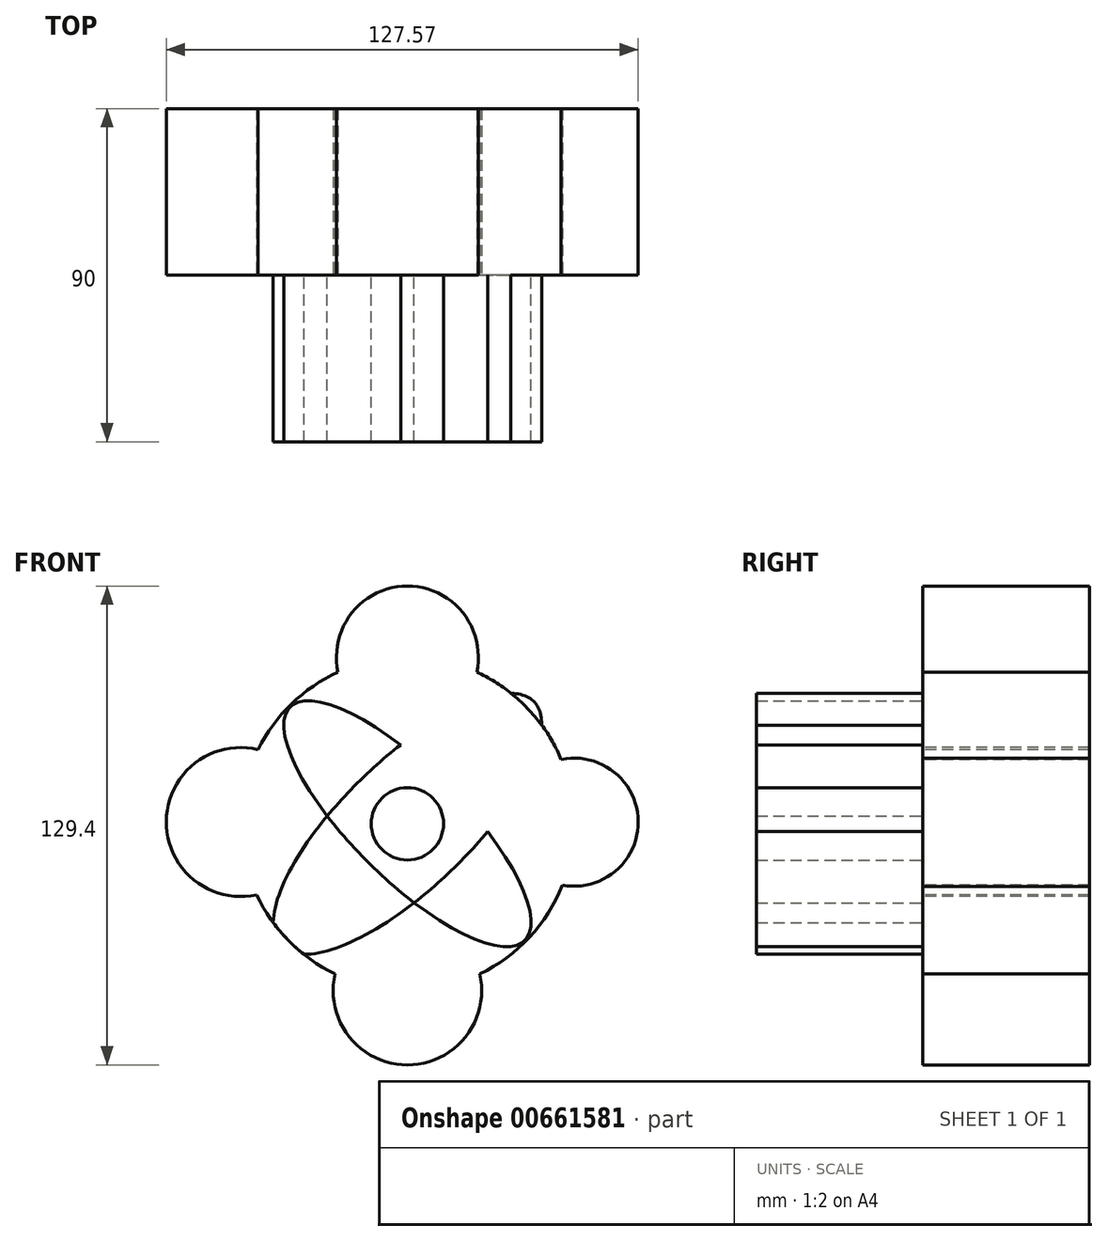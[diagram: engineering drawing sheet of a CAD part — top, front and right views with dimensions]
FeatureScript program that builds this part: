
annotation { "Feature Type Name" : "Feature", "Feature Type Description" : "" }
export const myFeature = defineFeature(function(context is Context, id is Id, definition is map)
    precondition{}
    {
        {
            var Q0;
            Q0=qCreatedBy(makeId("Front.planeOp"),FACE);
            var sketch = newSketch(context, id + "F0", { "sketchPlane" : qUnion([Q0])});
            skCircle(sketch, "E0", {"center": v(0, 0) * mm, "radius": 9.77 * mm});
            skPoint(sketch, "E1", {"position": v(0, 45) * mm});
            skPoint(sketch, "E2", {"position": v(45, 0) * mm});
            skPoint(sketch, "E3", {"position": v(0, -45) * mm});
            skPoint(sketch, "E4", {"position": v(-45, 0) * mm});
            skLineSegment(sketch, "E5", {"start": v(0, 0) * mm, "end": v(0, 45) * mm});
            skLineSegment(sketch, "E6", {"start": v(0, 0) * mm, "end": v(0, -45) * mm});
            skLineSegment(sketch, "E7", {"start": v(0, 0) * mm, "end": v(45, 0) * mm});
            skLineSegment(sketch, "E8", {"start": v(0, 0) * mm, "end": v(-45, 0) * mm});
            skSolve(sketch);
        }
        {
            var Q0;
            Q0=qCreatedBy(makeId("Front.planeOp"),FACE);
            var sketch = newSketch(context, id + "F1", { "sketchPlane" : qUnion([Q0])});
            skArc(sketch, "E9", {"start": v(0, 45.02) * mm, "mid": v(31.83, 31.83) * mm, "end": v(45.02, 0) * mm});
            skArc(sketch, "E10", {"start": v(0, 45.02) * mm, "mid": v(-31.83, 31.83) * mm, "end": v(-45.02, 0) * mm});
            skArc(sketch, "E11", {"start": v(-45.02, 0) * mm, "mid": v(-31.83, -31.83) * mm, "end": v(0, -45.02) * mm});
            skArc(sketch, "E12", {"start": v(0, -45.02) * mm, "mid": v(31.83, -31.83) * mm, "end": v(45.02, 0) * mm});
            skEllipse(sketch, "E13", {"center": v(0, 0) * mm, "majorRadius": 44.74 * mm, "minorRadius": 14.86 * mm, "majorAxis": v(-0.7, 0.7)});
            skEllipse(sketch, "E14", {"center": v(0, 0) * mm, "majorRadius": 47.54 * mm, "minorRadius": 17.34 * mm, "majorAxis": v(-0.72, -0.7)});
            skSolve(sketch);
        }
        {
            var Q0;
            {var subQ0=sQuery(id+"F1.wireOp",EDGE,"E14");var subQ1=sQuery(id+"F1.wireOp",EDGE,"E9");var subQ2=makeQuery(id+"F1.imprint","INTERSECT",VERTEX,{"disambiguationData":[OD(0.0)],"derivedFrom":[subQ1,subQ0]});Q0=makeQuery(id+"F1.imprint","IMPRINT",FACE,{"disambiguationData":[TD([[makeQuery(id+"F1.imprint","IMPRINT",EDGE,{"disambiguationData":[TD([[subQ2,-1.0]])],"derivedFrom":subQ1}),-1.0]])]});}
            var Q1;
            {var subQ0=sQuery(id+"F1.wireOp",EDGE,"E14");var subQ1=sQuery(id+"F1.wireOp",EDGE,"E11");var subQ2=makeQuery(id+"F1.imprint","INTERSECT",VERTEX,{"disambiguationData":[OD(0.0)],"derivedFrom":[subQ1,subQ0]});Q1=makeQuery(id+"F1.imprint","IMPRINT",FACE,{"disambiguationData":[TD([[makeQuery(id+"F1.imprint","IMPRINT",EDGE,{"disambiguationData":[TD([[subQ2,-1.0]])],"derivedFrom":subQ1}),1.0]])]});}
            var Q2;
            {var subQ0=sQuery(id+"F1.wireOp",EDGE,"E14");var subQ1=sQuery(id+"F1.wireOp",EDGE,"E13");var subQ2=makeQuery(id+"F1.imprint","INTERSECT",VERTEX,{"disambiguationData":[OD(1.0)],"derivedFrom":[subQ1,subQ0]});Q2=makeQuery(id+"F1.imprint","IMPRINT",FACE,{"disambiguationData":[TD([[makeQuery(id+"F1.imprint","IMPRINT",EDGE,{"disambiguationData":[TD([[subQ2,1.0]])],"derivedFrom":subQ1}),1.0]])]});}
            var Q3;
            {var subQ0=sQuery(id+"F1.wireOp",EDGE,"E14");var subQ1=sQuery(id+"F1.wireOp",EDGE,"E13");var subQ2=makeQuery(id+"F1.imprint","INTERSECT",VERTEX,{"disambiguationData":[OD(0.0)],"derivedFrom":[subQ1,subQ0]});Q3=makeQuery(id+"F1.imprint","IMPRINT",FACE,{"disambiguationData":[TD([[makeQuery(id+"F1.imprint","IMPRINT",EDGE,{"disambiguationData":[TD([[subQ2,-1.0]])],"derivedFrom":subQ1}),1.0]])]});}
            var Q4;
            Q4 = qSketchRegion(id + "F0", true);
            extrude(context, id + "F2", {"entities" : qUnion([Q0, Q1, Q2, Q3, Q4]), "depth" : 45 * mm, "offsetDistance" : 25.4 * mm});
        }
        {
            var Q0;
            Q0=qCreatedBy(makeId("Front.planeOp"),FACE);
            var sketch = newSketch(context, id + "F3", { "sketchPlane" : qUnion([Q0])});
            skCircle(sketch, "E15", {"center": v(0, 0) * mm, "radius": 45.07 * mm});
            skCircle(sketch, "E16", {"center": v(45.07, 0.43) * mm, "radius": 17.32 * mm});
            skCircle(sketch, "E17", {"center": v(0, 45.07) * mm, "radius": 19.18 * mm});
            skCircle(sketch, "E18", {"center": v(-45.07, 0.5) * mm, "radius": 20.13 * mm});
            skCircle(sketch, "E19", {"center": v(0, -45.07) * mm, "radius": 20.08 * mm});
            skSolve(sketch);
        }
        {
            var Q0;
            {var subQ0=sQuery(id+"F3.wireOp",EDGE,"E16");var subQ1=sQuery(id+"F3.wireOp",EDGE,"E15");var subQ2=makeQuery(id+"F3.imprint","INTERSECT",VERTEX,{"disambiguationData":[OD(0.0)],"derivedFrom":[subQ1,subQ0]});Q0=makeQuery(id+"F3.imprint","IMPRINT",FACE,{"disambiguationData":[TD([[makeQuery(id+"F3.imprint","IMPRINT",EDGE,{"disambiguationData":[TD([[subQ2,1.0]])],"derivedFrom":subQ1}),1.0]])]});}
            var Q1;
            {var subQ0=sQuery(id+"F3.wireOp",EDGE,"E19");var subQ1=sQuery(id+"F3.wireOp",EDGE,"E15");var subQ2=makeQuery(id+"F3.imprint","INTERSECT",VERTEX,{"disambiguationData":[OD(0.0)],"derivedFrom":[subQ1,subQ0]});Q1=makeQuery(id+"F3.imprint","IMPRINT",FACE,{"disambiguationData":[TD([[makeQuery(id+"F3.imprint","IMPRINT",EDGE,{"disambiguationData":[TD([[subQ2,-1.0]])],"derivedFrom":subQ1}),1.0]])]});}
            var Q2;
            {var subQ0=sQuery(id+"F3.wireOp",EDGE,"E17");var subQ1=sQuery(id+"F3.wireOp",EDGE,"E15");var subQ2=makeQuery(id+"F3.imprint","INTERSECT",VERTEX,{"disambiguationData":[OD(0.0)],"derivedFrom":[subQ1,subQ0]});Q2=makeQuery(id+"F3.imprint","IMPRINT",FACE,{"disambiguationData":[TD([[makeQuery(id+"F3.imprint","IMPRINT",EDGE,{"disambiguationData":[TD([[subQ2,-1.0]])],"derivedFrom":subQ1}),-1.0]])]});}
            var Q3;
            {var subQ0=sQuery(id+"F3.wireOp",EDGE,"E18");var subQ1=sQuery(id+"F3.wireOp",EDGE,"E15");var subQ2=makeQuery(id+"F3.imprint","INTERSECT",VERTEX,{"disambiguationData":[OD(0.0)],"derivedFrom":[subQ1,subQ0]});Q3=makeQuery(id+"F3.imprint","IMPRINT",FACE,{"disambiguationData":[TD([[makeQuery(id+"F3.imprint","IMPRINT",EDGE,{"disambiguationData":[TD([[subQ2,-1.0]])],"derivedFrom":subQ1}),-1.0]])]});}
            var Q4;
            {var subQ0=sQuery(id+"F3.wireOp",EDGE,"E16");var subQ1=sQuery(id+"F3.wireOp",EDGE,"E15");var subQ2=makeQuery(id+"F3.imprint","INTERSECT",VERTEX,{"disambiguationData":[OD(0.0)],"derivedFrom":[subQ1,subQ0]});Q4=makeQuery(id+"F3.imprint","IMPRINT",FACE,{"disambiguationData":[TD([[makeQuery(id+"F3.imprint","IMPRINT",EDGE,{"disambiguationData":[TD([[subQ2,1.0]])],"derivedFrom":subQ1}),-1.0]])]});}
            var Q5;
            {var subQ0=sQuery(id+"F3.wireOp",EDGE,"E18");var subQ1=sQuery(id+"F3.wireOp",EDGE,"E15");var subQ2=makeQuery(id+"F3.imprint","INTERSECT",VERTEX,{"disambiguationData":[OD(0.0)],"derivedFrom":[subQ1,subQ0]});Q5=makeQuery(id+"F3.imprint","IMPRINT",FACE,{"disambiguationData":[TD([[makeQuery(id+"F3.imprint","IMPRINT",EDGE,{"disambiguationData":[TD([[subQ2,-1.0]])],"derivedFrom":subQ1}),1.0]])]});}
            var Q6;
            {var subQ0=sQuery(id+"F3.wireOp",EDGE,"E19");var subQ1=sQuery(id+"F3.wireOp",EDGE,"E15");var subQ2=makeQuery(id+"F3.imprint","INTERSECT",VERTEX,{"disambiguationData":[OD(0.0)],"derivedFrom":[subQ1,subQ0]});Q6=makeQuery(id+"F3.imprint","IMPRINT",FACE,{"disambiguationData":[TD([[makeQuery(id+"F3.imprint","IMPRINT",EDGE,{"disambiguationData":[TD([[subQ2,-1.0]])],"derivedFrom":subQ1}),-1.0]])]});}
            var Q7;
            {var subQ1=sQuery(id+"F3.wireOp",EDGE,"E15");var subQ8=sQuery(id+"F3.wireOp",EDGE,"E17");var subQ11=makeQuery(id+"F3.imprint","INTERSECT",VERTEX,{"disambiguationData":[OD(0.0)],"derivedFrom":[subQ1,subQ8]});Q7=makeQuery(id+"F3.imprint","IMPRINT",FACE,{"disambiguationData":[TD([[makeQuery(id+"F3.imprint","IMPRINT",EDGE,{"disambiguationData":[TD([[subQ11,1.0]])],"derivedFrom":subQ1}),1.0]])]});}
            var Q8;
            {var subQ0=sQuery(id+"F3.wireOp",EDGE,"E17");var subQ1=sQuery(id+"F3.wireOp",EDGE,"E15");var subQ2=makeQuery(id+"F3.imprint","INTERSECT",VERTEX,{"disambiguationData":[OD(0.0)],"derivedFrom":[subQ1,subQ0]});Q8=makeQuery(id+"F3.imprint","IMPRINT",FACE,{"disambiguationData":[TD([[makeQuery(id+"F3.imprint","IMPRINT",EDGE,{"disambiguationData":[TD([[subQ2,-1.0]])],"derivedFrom":subQ1}),1.0]])]});}
            extrude(context, id + "F4", {"entities" : qUnion([Q0, Q1, Q2, Q3, Q4, Q5, Q6, Q7, Q8]), "oppositeDirection" : true, "depth" : 45 * mm, "offsetDistance" : 25.4 * mm});
        }
    });
